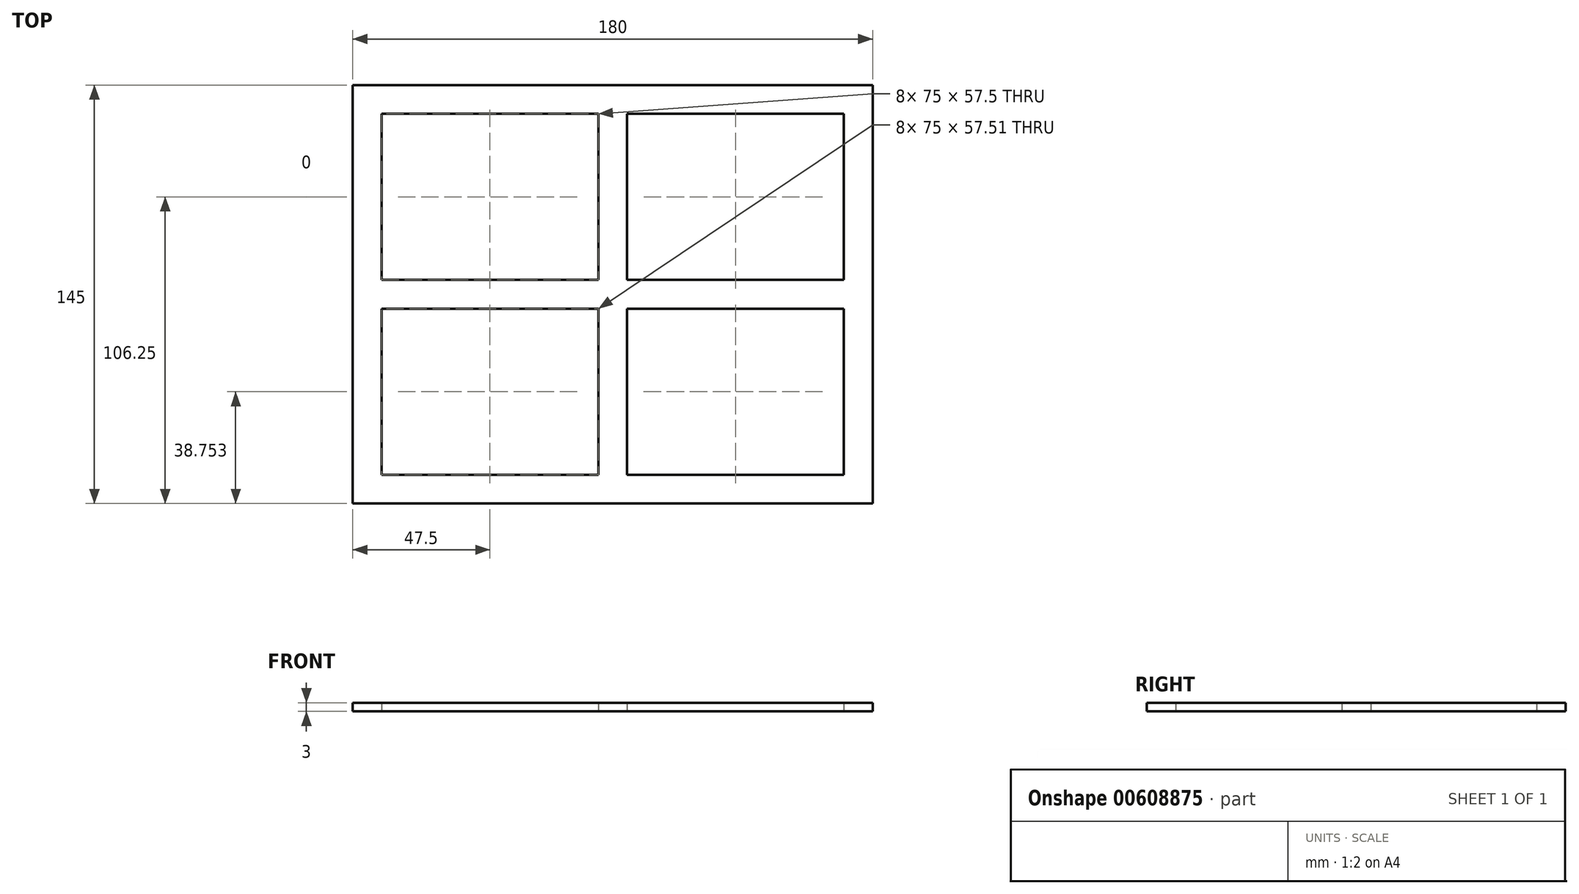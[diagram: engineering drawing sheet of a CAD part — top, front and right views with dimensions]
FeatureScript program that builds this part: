
annotation { "Feature Type Name" : "Feature", "Feature Type Description" : "" }
export const myFeature = defineFeature(function(context is Context, id is Id, definition is map)
    precondition{}
    {
        {
            var Q0;
            Q0=qCreatedBy(makeId("Top.planeOp"),FACE);
            var sketch = newSketch(context, id + "F0", { "sketchPlane" : qUnion([Q0])});
            skLineSegment(sketch, "E0.bottom", {"start": v(90, -72.5) * mm, "end": v(-90, -72.5) * mm});
            skLineSegment(sketch, "E0.top", {"start": v(90, 72.5) * mm, "end": v(-90, 72.5) * mm});
            skLineSegment(sketch, "E0.left", {"start": v(90, -72.5) * mm, "end": v(90, 72.5) * mm});
            skLineSegment(sketch, "E0.right", {"start": v(-90, -72.5) * mm, "end": v(-90, 72.5) * mm});
            skPoint(sketch, "E0.middle", {"position": v(0, 0) * mm});
            skLineSegment(sketch, "E1.0", {"start": v(-80, -62.5) * mm, "end": v(-80, -5) * mm});
            skLineSegment(sketch, "E1.1", {"start": v(80, -62.5) * mm, "end": v(5, -62.5) * mm});
            skLineSegment(sketch, "E1.2", {"start": v(80, -62.5) * mm, "end": v(80, -5) * mm});
            skLineSegment(sketch, "E1.3", {"start": v(80, 62.5) * mm, "end": v(5, 62.5) * mm});
            skLineSegment(sketch, "E2", {"start": v(-80, 62.5) * mm, "end": v(-5, 62.5) * mm, "construction": true});
            skLineSegment(sketch, "E3", {"start": v(80, 62.5) * mm, "end": v(5, 62.5) * mm, "construction": true});
            skLineSegment(sketch, "E4", {"start": v(-80, 62.5) * mm, "end": v(-80, 5) * mm, "construction": true});
            skLineSegment(sketch, "E5", {"start": v(-80, -62.5) * mm, "end": v(-80, -5) * mm, "construction": true});
            skLineSegment(sketch, "E6.left", {"start": v(-5, 62.5) * mm, "end": v(-5, 5) * mm});
            skLineSegment(sketch, "E6.right", {"start": v(5, 62.5) * mm, "end": v(5, 5) * mm});
            skLineSegment(sketch, "E7.bottom", {"start": v(-80, 5) * mm, "end": v(-5, 5) * mm});
            skLineSegment(sketch, "E7.top", {"start": v(-80, -5) * mm, "end": v(-5, -5) * mm});
            skLineSegment(sketch, "E8.trimOffspring", {"start": v(-80, 5) * mm, "end": v(-80, 62.5) * mm});
            skLineSegment(sketch, "E9.trimOffspring", {"start": v(-5, -5) * mm, "end": v(-5, -62.5) * mm});
            skLineSegment(sketch, "E10.trimOffspring", {"start": v(5, -5) * mm, "end": v(5, -62.5) * mm});
            skLineSegment(sketch, "E11.trimOffspring", {"start": v(-5, 62.5) * mm, "end": v(-80, 62.5) * mm});
            skLineSegment(sketch, "E12.trimOffspring", {"start": v(5, 5) * mm, "end": v(80, 5) * mm});
            skLineSegment(sketch, "E13.trimOffspring", {"start": v(5, -5) * mm, "end": v(80, -5) * mm});
            skLineSegment(sketch, "E14.trimOffspring", {"start": v(-5, -62.5) * mm, "end": v(-80, -62.5) * mm});
            skLineSegment(sketch, "E15.trimOffspring", {"start": v(80, 5) * mm, "end": v(80, 62.5) * mm});
            skSolve(sketch);
        }
        {
            var Q0;
            Q0 = qSketchRegion(id + "F0", true);
            extrude(context, id + "F1", {"entities" : qUnion([Q0]), "depth" : 3 * mm, "offsetDistance" : 25 * mm});
        }
    });
